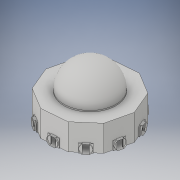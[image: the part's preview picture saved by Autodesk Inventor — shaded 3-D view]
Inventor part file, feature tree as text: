
AUTODESK INVENTOR PART (.ipt)
format: ipt  version: 2017 (Build 210142000, 142)  size: 407,040 bytes
history: native  units: in
note: dims shown in document units (in); Inventor stores cm internally (conversion verified against a paired STEP export)
features: sketch x7, extrude x6, other x3, mirror x1, pattern_circular x1, delete_face x1
ambient origin geometry x8: Origin, YZ Plane, XZ Plane, XY Plane, X Axis, Y Axis, Z Axis, Center Point
bodies: Solid1 (feature_tree)
feature tree (19):
  extrude  "bace"  Depth=1.0in TaperAngle=0.0deg
  extrude  "bace wall"  Depth=20.0in TaperAngle=0.0deg
  extrude  "bace cieiling"  Depth=6.6667in
  other  "dome work plane"
  other  "dome"
  extrude  "door frame"  Depth=1.0in TaperAngle=0.0deg
  extrude  "corridor connection"  Depth=0.25in
  extrude  "left door slot"  Depth=2.0in
  other  "door slot mirror"
  mirror  "other side of the door"
  pattern_circular  "Circular Pattern1"  [2 undecoded]
  delete_face  "Delete Face1"
  sketch  "Sketch1"  dims[d0=62.0in d1=1.0in d2=0.0in]
  sketch  "Sketch2"  dims[d4=1.0in d5=20.0in d6=0.0in]
  sketch  "Sketch3"  dims[d8=1.0in d9=0.0in d14=6.6667in d15=4.0in]
  sketch  "Sketch7"  dims[d16=2.0in d17=6.6667in d18=1.0in d19=0.0in]
  sketch  "Sketch8"  dims[d20=1.0in d21=0.0in d22=0.25in d23=0.5in d24=6.6667in]
  sketch  "Sketch9"  dims[d25=2.0in d26=0.0in d28=40.0in]
  sketch  "Sketch10"  dims[d32=20.0in d33=21.0in d34=90.0deg d35=3.937in d36=360.0deg]
note: 2 required parameter values undecoded (feature->parameter linkage not recoverable at this tier; creation-order binding heuristic only, values carry confidence <= 0.55)
